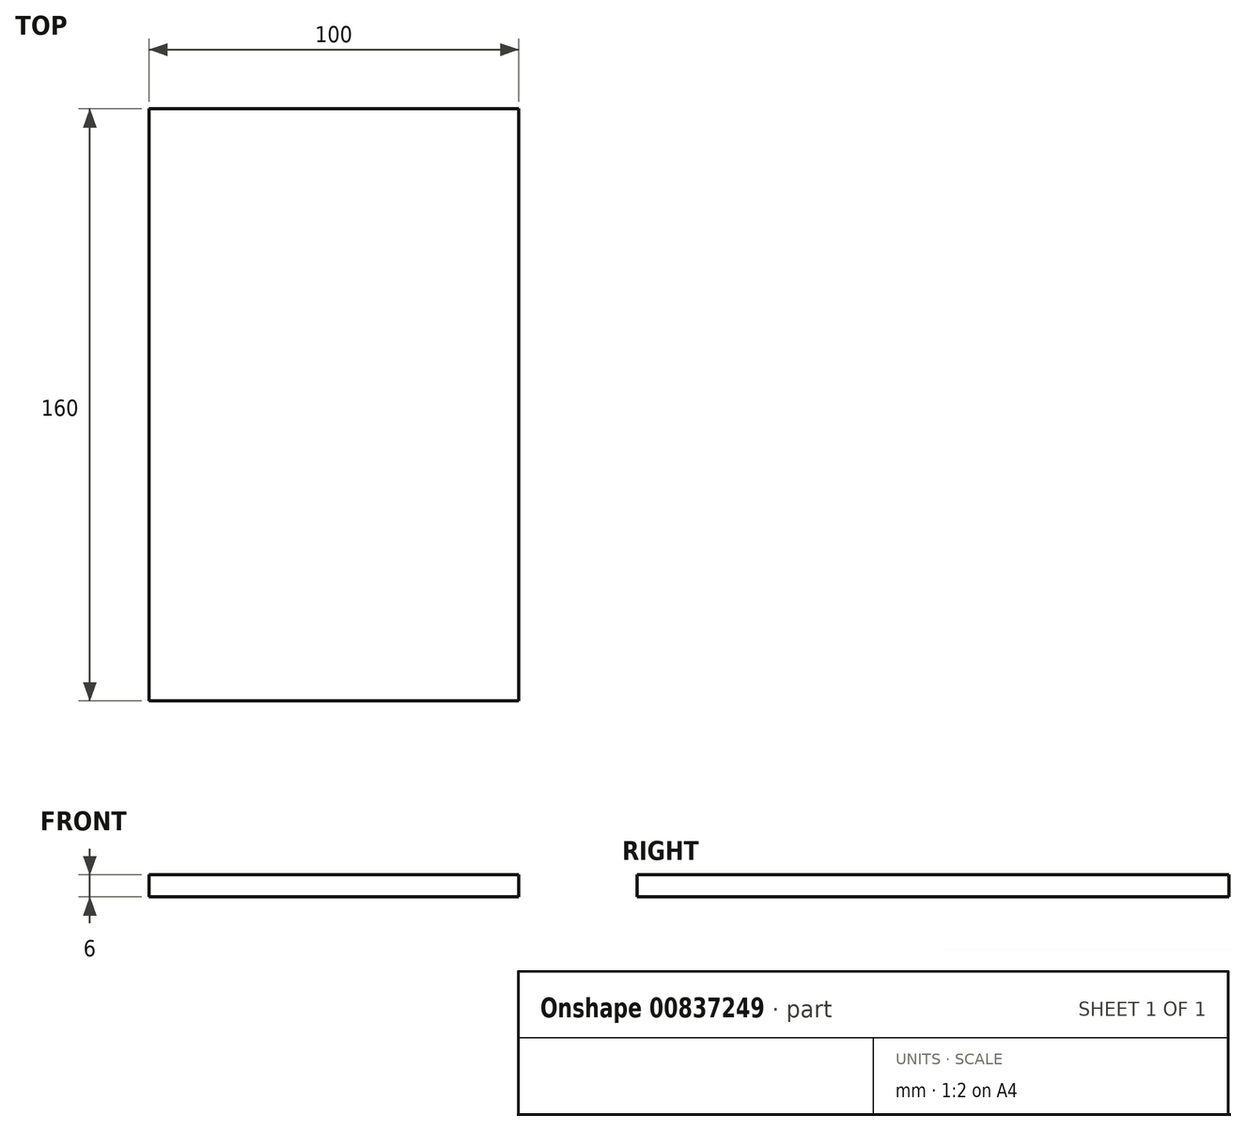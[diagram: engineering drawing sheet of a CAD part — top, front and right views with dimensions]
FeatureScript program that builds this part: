
annotation { "Feature Type Name" : "Feature", "Feature Type Description" : "" }
export const myFeature = defineFeature(function(context is Context, id is Id, definition is map)
    precondition{}
    {
        {
            var Q0;
            Q0=qCreatedBy(makeId("Top.planeOp"),FACE);
            var sketch = newSketch(context, id + "F0", { "sketchPlane" : qUnion([Q0])});
            skLineSegment(sketch, "E0.bottom", {"start": v(50, 80) * mm, "end": v(-50, 80) * mm});
            skLineSegment(sketch, "E0.top", {"start": v(50, -80) * mm, "end": v(-50, -80) * mm});
            skLineSegment(sketch, "E0.left", {"start": v(50, 80) * mm, "end": v(50, -80) * mm});
            skLineSegment(sketch, "E0.right", {"start": v(-50, 80) * mm, "end": v(-50, -80) * mm});
            skPoint(sketch, "E0.middle", {"position": v(0, 0) * mm});
            skSolve(sketch);
        }
        {
            var Q0;
            Q0 = qSketchRegion(id + "F0", true);
            extrude(context, id + "F1", {"entities" : qUnion([Q0]), "depth" : 6 * mm, "offsetDistance" : 25.4 * mm});
        }
    });
